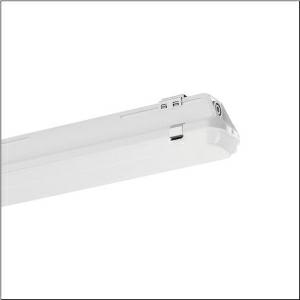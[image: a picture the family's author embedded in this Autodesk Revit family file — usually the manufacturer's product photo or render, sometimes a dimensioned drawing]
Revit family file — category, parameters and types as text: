
# Revit family: monsun_r__21_51fb20mp480b_5a94
name_source: partatom
category: Lighting Fixtures
units: mm (PartAtom-declared; Revit-internal decimal feet)

## family parameters
Cut with Voids When Loaded = No
Host = Face
Light Source = No
Part Type = Normal
Room Calculation Point = No
Round Connector Dimension = Use Diameter
Shared = No

## types (1)
- --- (1 x LED, 7370 lm, 53.6 W, 4000K)
    Apparent Load = 54 VA
    CIE Flux Codes = 45 75 93 94 100
    Color Rendering = 80
    Color Temperature = 4000K
    Default Elevation = 1800 mm
    Description = Monsun® 21, damp-proof luminaire, chain hanger, primary optical cover: enclosure, of PC, light emission: direct distribution, primary light characteristic: symmetric, installation type: suspended mounting, surface-mounted, horizontal mounting, vertical mounting, LED, rated luminous flux: 7.370lm, luminous efficacy: 138lm/W, light colour: 840, colour temperature: 4000K, control gear: ECG, with terminal, 3-pole, max. 2.5mm², mains connection: 220..240V, AC, 50/60Hz, rated input power: 54W, housing, of glass-fibre reinforced polyester, uncoated, bright grey, length: 1.590mm, width: 90mm, height: 88mm, clip for enclosure, of stainless steel (V2A), ceiling mounting element, of stainless steel (V2A), chain hanger, of stainless steel (V2A), protection rating (complete): IP66, insulation class (complete): insulation class I (protective earthing), certification: CE, ENEC, VDE, UKCA, protection symbol: D, impact resistance: IK08, permissible operating ambient temperature: -25..+35°C, standard: EN 50419, EN 60598-2-1, corresponds to IFS (International Featured Standards) requirements for safety and quality in the food industry, for indoor or canopied outdoor use, no direct snow, no direct sun, no direct rain, packaging unit: 1 piece
    Height = 89 mm
    Lamp = 1 x LED
    Lamp Light Flux = 7370 lm
    Lamp Power = 53.6 W
    Lamp count = 1
    Length = 1590 mm
    Luminous efficacy = 138 lm/W
    Manufacturer = Siteco
    ModVariant = No
    Model = 51FB20MP480B
    Mounting Place = Ceiling
    Mounting Type = Pendant
    Number of Poles = 1
    OnlyDefault = Yes
    Power Factor = 1
    Product Name = Monsun® 21
    Product group = damp-proof luminaire | ceiling pendant
    ProductGroupID = 908
    Protection Class = Protection class I
    Protection Degree = IP 66
    RLX_Detail_Level = 1
    RlxData = <blob elided: 89625 chars, md5=107c5eeb>
    Socket = socket
    Standby Power = 0 W
    System Light Flux = 7370 lm
    System Power = 54 W
    Type Comments = factory setting: luminous flux: 100 % | (A | C | E) | 121 mA
    Type Image = l_1006717.jpg
    URL = http://relux.com
    VarID = @adj_056851
    Voltage = 0 V
    Weight = 0.00 kg
    Width = 90 mm

## geometry (parser evidence)
native form markers: Blend x4, Sweep x15
no freeform markers — native parametric forms only
